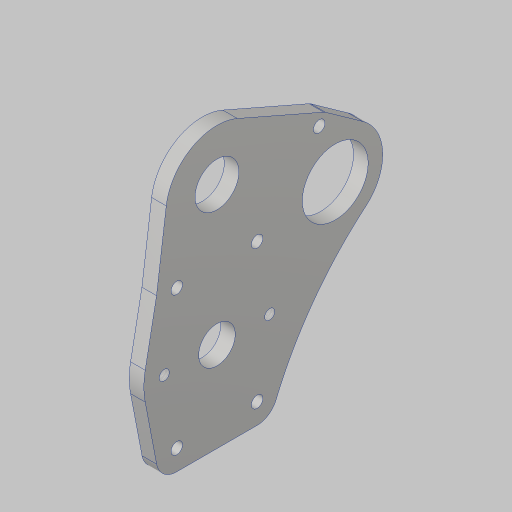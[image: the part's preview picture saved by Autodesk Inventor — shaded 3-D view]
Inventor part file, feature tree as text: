
AUTODESK INVENTOR PART (.ipt)
format: ipt  version: 2023.5 (Build 275446000, 446)  size: 208,896 bytes
history: native  units: in
note: dims shown in document units (in); Inventor stores cm internally (conversion verified against a paired STEP export)
features: sketch x4, extrude x2, hole x2
ambient origin geometry x8: Origin, YZ Plane, XZ Plane, XY Plane, X Axis, Y Axis, Z Axis, Center Point
bodies: Solid1 (feature_tree)
feature tree (8):
  sketch  "Sketch1"  dims[d0=3.0in d1=2.2in]
  sketch  "Sketch2"  dims[d2=3.0in d3=2.375in]
  extrude  "Extrusion1"  Depth=2.2in
  hole  "Hole3"  [1 undecoded]
  extrude  "Extrusion5"  Depth=0.201in
  hole  "Hole4"  [1 undecoded]
  sketch  "Sketch6"  dims[d4=1.375in d5=0.201in]
  sketch  "Sketch7"  dims[d6=0.201in d7=0.201in d8=0.201in d9=1.0in d12=2.3622in d14=360.0deg d16=1.125in d17=2.246in d19=2.5in d20=0.75in d23=0.25in d24=0.25in d25=0.0in d41=1.1811in d43=360.0deg d45=0.375in d46=0.385in d47=0.375in d49=0.196in d50=0.75in d51=0.385in d52=0.25in d53=0.5635in d54=1.0in d55=0.8108in d56=2.0in d57=0.25in d58=1.75in d60=3.0in d65=2.362in d66=0.25in d75=0.6in d76=2.0in d77=1.75in d78=0.875in d79=5.5in d80=0.625in d81=0.25in d82=0.0in d83=1.8028in d84=0.171in d85=0.432in d86=0.385in d87=0.25in d88=0.5635in d89=1.0in d90=0.8108in]
note: 2 required parameter values undecoded (feature->parameter linkage not recoverable at this tier; creation-order binding heuristic only, values carry confidence <= 0.55)
